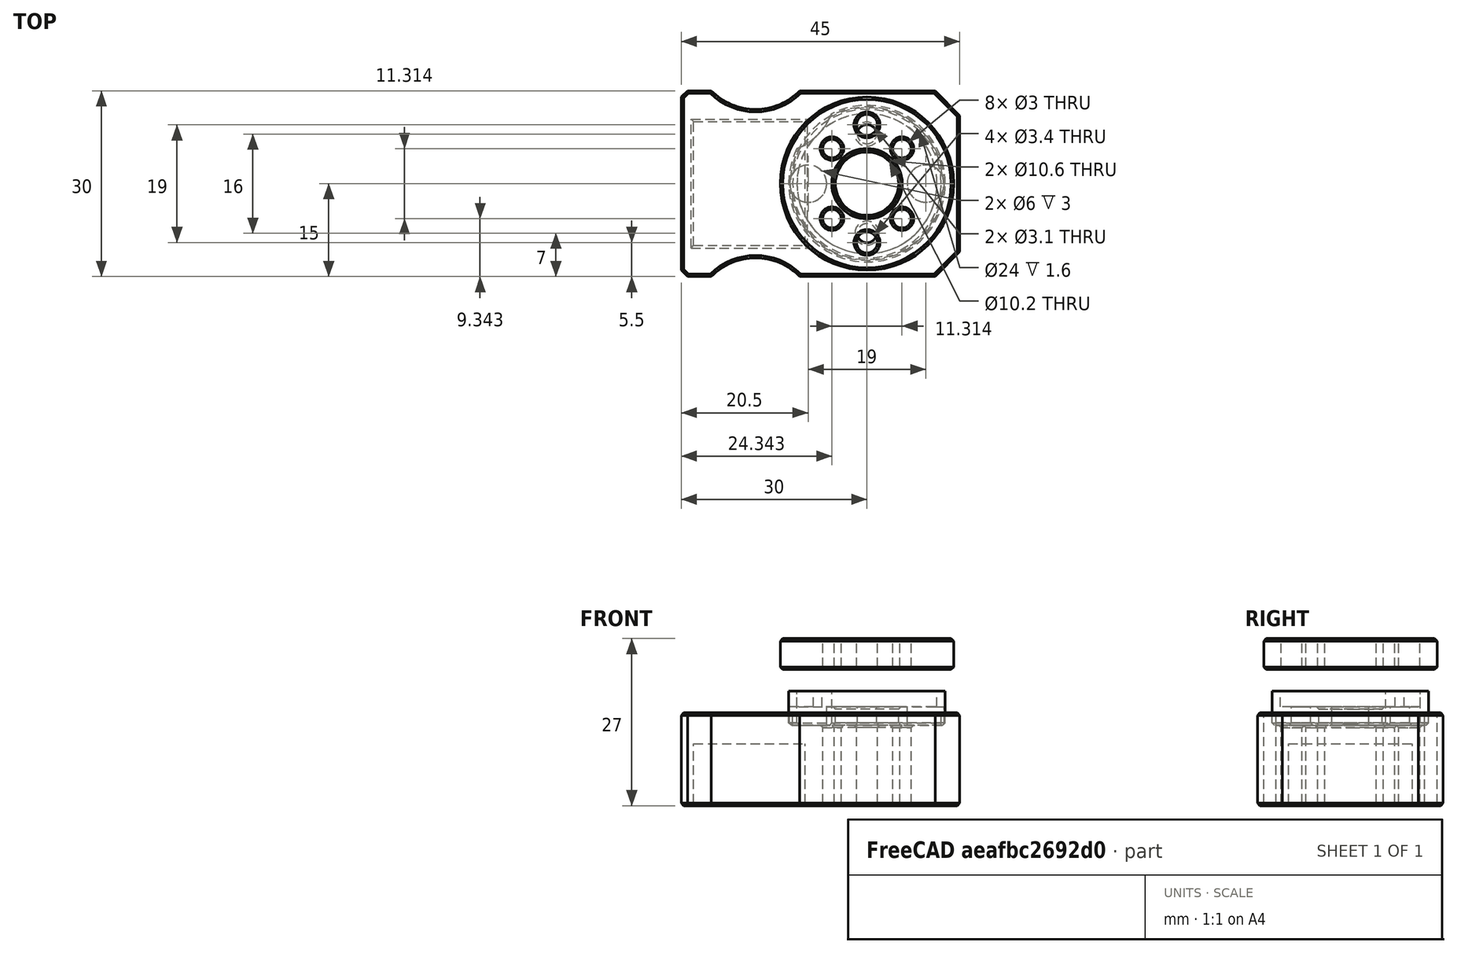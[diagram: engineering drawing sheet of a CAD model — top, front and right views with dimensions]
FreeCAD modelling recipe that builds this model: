
FCSTD DOCUMENT  (FreeCAD 0.18R14555 (Git shallow))
Label: lead-screw-nut-drill-template
License: All rights reserved
LicenseURL: http://en.wikipedia.org/wiki/All_rights_reserved
objects: Part::Cylinder×11, Part::Cut×5, Part::MultiFuse×5, Part::Chamfer×5, Part::Feature×2, Part::Box×2
note: 30 computed .brp shape members not serialized (recipe doc carries the construction recipe); baked Part::Feature solids carry a one-line shape summary decoded from their .brp

FEATURE [Part::Feature] Cut017021010004016001  label="ref"
  Placement = pos=(0,0,0) rot=(0,0,-1;0.785398rad)
  shape: bbox 25.3 x 25.3 x 5.5 mm, 19 faces (baked)
FEATURE [Part::Cylinder] Cylinder  label="drill-clearance-1"
  Angle = 360
  AttacherType = Attacher::AttachEngine3D
  Height = 20
  Placement = pos=(0,9.5,0) rot=(0,0,1;0rad)
  Radius = 1.7
FEATURE [Part::Cylinder] Cylinder001  label="drill-clearance-2"
  Angle = 360
  AttacherType = Attacher::AttachEngine3D
  Height = 20
  Placement = pos=(0,-9.5,0) rot=(0,0,1;0rad)
  Radius = 1.7
FEATURE [Part::Cylinder] Cylinder004  label="Cylinder"
  Angle = 360
  AttacherType = Attacher::AttachEngine3D
  Height = 2
  Radius = 12
FEATURE [Part::Box] Box  label="Cube"
  AttacherType = Attacher::AttachEngine3D
  Height = 15
  Length = 45
  Placement = pos=(-30,-15,-13) rot=(0,0,1;0rad)
  Width = 30
FEATURE [Part::Cylinder] Cylinder005  label="Cylinder001"
  Angle = 360
  AttacherType = Attacher::AttachEngine3D
  Height = 20
  Radius = 5.3
FEATURE [Part::Cut] Cut
  Base = -> Box
  Tool = -> Cylinder004
FEATURE [Part::Cylinder] Cylinder006  label="Cylinder002"
  Angle = 360
  AttacherType = Attacher::AttachEngine3D
  Height = 20
  Placement = pos=(-18,-22,0) rot=(0,0,1;0rad)
  Radius = 10
FEATURE [Part::Cylinder] Cylinder007  label="Cylinder003"
  Angle = 360
  AttacherType = Attacher::AttachEngine3D
  Height = 20
  Placement = pos=(-18,22,0) rot=(0,0,1;0rad)
  Radius = 10
FEATURE [Part::MultiFuse] Fusion002004002
  Placement = pos=(0,0,-16) rot=(0,0,1;0rad)
  Shapes = -> [Cylinder006,Cylinder007]
FEATURE [Part::Box] Box001  label="Cube001"
  AttacherType = Attacher::AttachEngine3D
  Height = 10
  Length = 18
  Placement = pos=(-28,-10,-13) rot=(0,0,1;0rad)
  Width = 20
FEATURE [Part::Cylinder] Cylinder008  label="Cylinder004"
  Angle = 360
  AttacherType = Attacher::AttachEngine3D
  Height = 5
  Radius = 14
FEATURE [Part::MultiFuse] Fusion
  Shapes = -> [Cylinder,Cylinder005,Cylinder001]
FEATURE [Part::Cylinder] Cylinder009  label="Cylinder005"
  Angle = 360
  AttacherType = Attacher::AttachEngine3D
  Height = 20
  Placement = pos=(0,8,0) rot=(0,0,1;0rad)
  Radius = 1.5
FEATURE [Part::Cylinder] Cylinder010  label="Cylinder006"
  Angle = 360
  AttacherType = Attacher::AttachEngine3D
  Height = 20
  Placement = pos=(8,0,0) rot=(0,0,1;0rad)
  Radius = 1.5
FEATURE [Part::Cylinder] Cylinder011  label="Cylinder007"
  Angle = 360
  AttacherType = Attacher::AttachEngine3D
  Height = 20
  Placement = pos=(-8,0,0) rot=(0,0,1;0rad)
  Radius = 1.5
FEATURE [Part::Cylinder] Cylinder012  label="Cylinder008"
  Angle = 360
  AttacherType = Attacher::AttachEngine3D
  Height = 20
  Placement = pos=(0,-8,0) rot=(0,0,1;0rad)
  Radius = 1.5
FEATURE [Part::MultiFuse] Fusion002004003
  Placement = pos=(0,0,0) rot=(0,0,-1;0.785398rad)
  Shapes = -> [Cylinder012,Cylinder010,Cylinder009,Cylinder011]
FEATURE [Part::MultiFuse] Fusion002004004
  Shapes = -> [Fusion]
FEATURE [Part::MultiFuse] Fusion002004005
  Placement = pos=(0,0,-17) rot=(0,0,1;0rad)
  Shapes = -> [Fusion002004003,Fusion002004004]
FEATURE [Part::Feature] Fusion002004005001  label="Fusion002004006"
  shape: bbox 14.31 x 22.4 x 20 mm, 21 faces, 7 solids (baked)
FEATURE [Part::Cut] Cut017021010004016006
  Base = -> Cut
  Tool = -> Fusion002004005
FEATURE [Part::Cut] Cut017021010004016007
  Base = -> Cut017021010004016006
  Tool = -> Box001
FEATURE [Part::Cut] Cut017021010004016008
  Base = -> Cut017021010004016007
  Tool = -> Fusion002004002
FEATURE [Part::Chamfer] Chamfer
  Base = -> Cut017021010004016008
  Edges = 2 edges r=1: [Edge1,Edge3]
FEATURE [Part::Chamfer] Chamfer004
  Base = -> Chamfer
  Edges = 2 edges r=4: [Edge39,Edge40]
FEATURE [Part::Chamfer] Chamfer005
  Base = -> Chamfer004
  Edges = 36 edges r=0.4: [Edge1,Edge2,Edge3,Edge4,Edge5,Edge6,Edge7,Edge8,Edge9,Edge10,Edge11,Edge12,Edge13,Edge14,Edge17,Edge19,Edge22,Edge23,Edge25,Edge27,Edge29,Edge32,Edge34,Edge35,Edge37,Edge40,Edge41,Edge42,Edge43,Edge44,Edge45,Edge46,Edge47,Edge48,Edge49,Edge50]
FEATURE [Part::Chamfer] Chamfer006  label="base"
  Base = -> Chamfer005
  Edges = 7 edges r=0.4: [Edge90,Edge91,Edge92,Edge93,Edge94,Edge95,Edge96]
FEATURE [Part::Cut] Cut017021010004016009
  Base = -> Cylinder008
  Tool = -> Fusion002004005001
FEATURE [Part::Chamfer] Chamfer007  label="cap"
  Base = -> Cut017021010004016009
  Edges = 16 edges r=0.4: [Edge1,Edge3,Edge4,Edge5,Edge6,Edge7,Edge8,Edge9,Edge10,Edge11,Edge12,Edge13,Edge14,Edge15,Edge16,Edge17]
  Placement = pos=(0,0,9) rot=(0,0,1;0rad)
